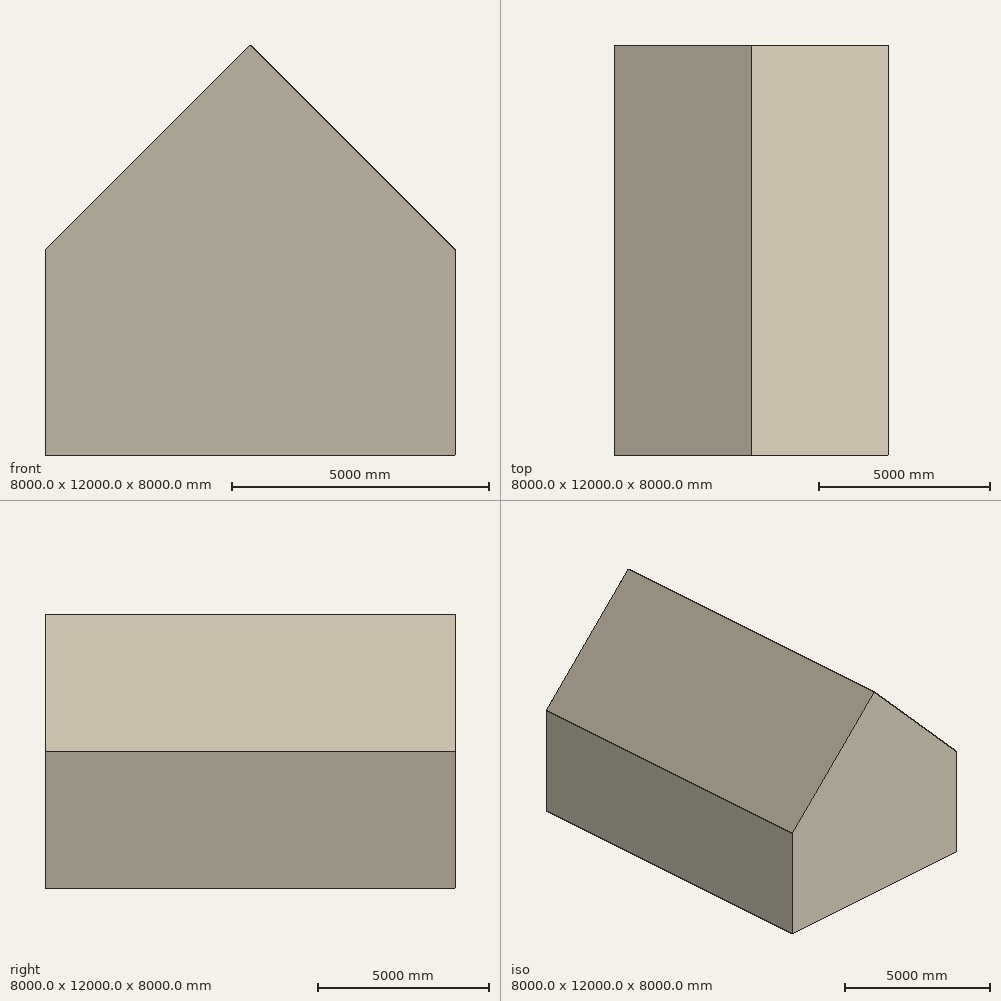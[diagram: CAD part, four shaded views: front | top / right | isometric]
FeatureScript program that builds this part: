
annotation { "Feature Type Name" : "Feature", "Feature Type Description" : "" }
export const myFeature = defineFeature(function(context is Context, id is Id, definition is map)
    precondition{}
    {
        {
            var Q0;
            Q0=qCreatedBy(makeId("Front.planeOp"),FACE);
            var sketch = newSketch(context, id + "F0", { "sketchPlane" : qUnion([Q0])});
            skLineSegment(sketch, "E0.bottom", {"start": v(0, 0) * mm, "end": v(8000, 0) * mm});
            skLineSegment(sketch, "E0.top", {"start": v(0, -4000) * mm, "end": v(8000, -4000) * mm});
            skLineSegment(sketch, "E0.left", {"start": v(0, 0) * mm, "end": v(0, -4000) * mm});
            skLineSegment(sketch, "E0.right", {"start": v(8000, 0) * mm, "end": v(8000, -4000) * mm});
            skLineSegment(sketch, "E1", {"start": v(4000, 0) * mm, "end": v(4000, 4000) * mm});
            skLineSegment(sketch, "E2", {"start": v(4000, 4000) * mm, "end": v(0, 0) * mm});
            skLineSegment(sketch, "E3", {"start": v(4000, 4000) * mm, "end": v(8000, 0) * mm});
            skSolve(sketch);
        }
        {
            var Q0;
            Q0=makeQuery(id+"F0.imprint","IMPRINT",FACE,{"disambiguationData":[TD([[makeQuery(id+"F0.imprint","IMPRINT",EDGE,{"derivedFrom":sQuery(id+"F0.wireOp",EDGE,"E0.top")}),1.0]])]});
            var Q1;
            {var subQ2=sQuery(id+"F0.wireOp",EDGE,"E1");Q1=makeQuery(id+"F0.imprint","IMPRINT",FACE,{"disambiguationData":[TD([[makeQuery(id+"F0.imprint","IMPRINT",EDGE,{"derivedFrom":subQ2}),1.0]])]});}
            var Q2;
            {var subQ2=sQuery(id+"F0.wireOp",EDGE,"E1");Q2=makeQuery(id+"F0.imprint","IMPRINT",FACE,{"disambiguationData":[TD([[makeQuery(id+"F0.imprint","IMPRINT",EDGE,{"derivedFrom":subQ2}),-1.0]])]});}
            extrude(context, id + "F1", {"entities" : qUnion([Q0, Q1, Q2]), "depth" : 12000 * mm});
        }
    });
